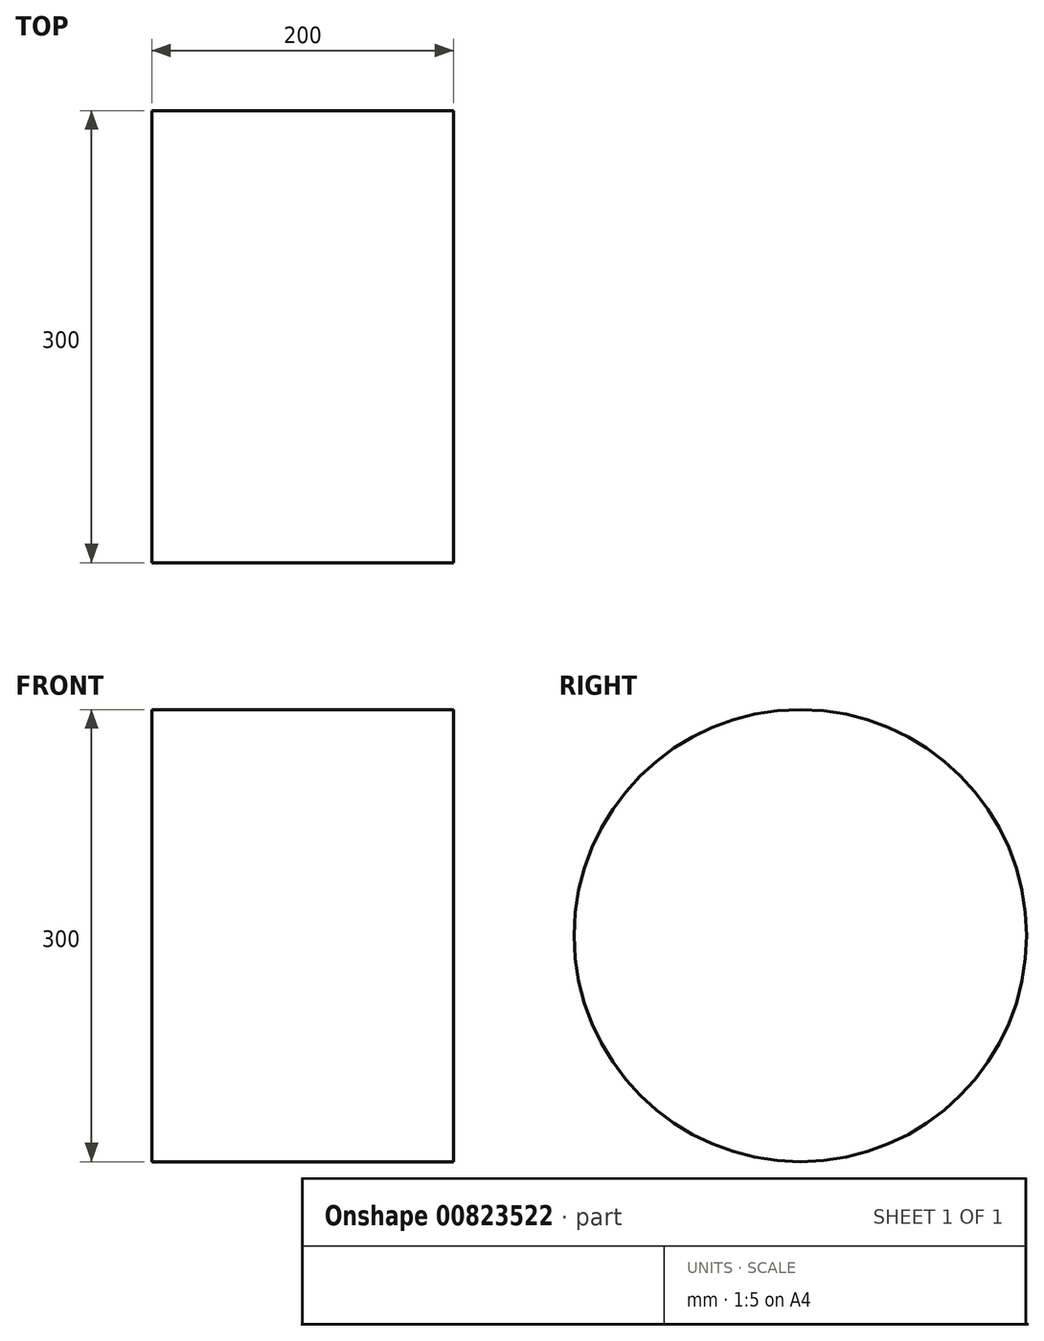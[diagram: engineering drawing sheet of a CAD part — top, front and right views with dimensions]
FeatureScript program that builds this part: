
annotation { "Feature Type Name" : "Feature", "Feature Type Description" : "" }
export const myFeature = defineFeature(function(context is Context, id is Id, definition is map)
    precondition{}
    {
        {
            var Q0;
            Q0=qCreatedBy(makeId("Right.planeOp"),FACE);
            var sketch = newSketch(context, id + "F0", { "sketchPlane" : qUnion([Q0])});
            skCircle(sketch, "E0", {"center": v(-0.77, -0.15) * mm, "radius": 150 * mm});
            skSolve(sketch);
        }
        {
            var Q0;
            Q0 = qSketchRegion(id + "F0", true);
            extrude(context, id + "F1", {"entities" : qUnion([Q0]), "depth" : 200 * mm, "offsetDistance" : 25 * mm});
        }
    });
